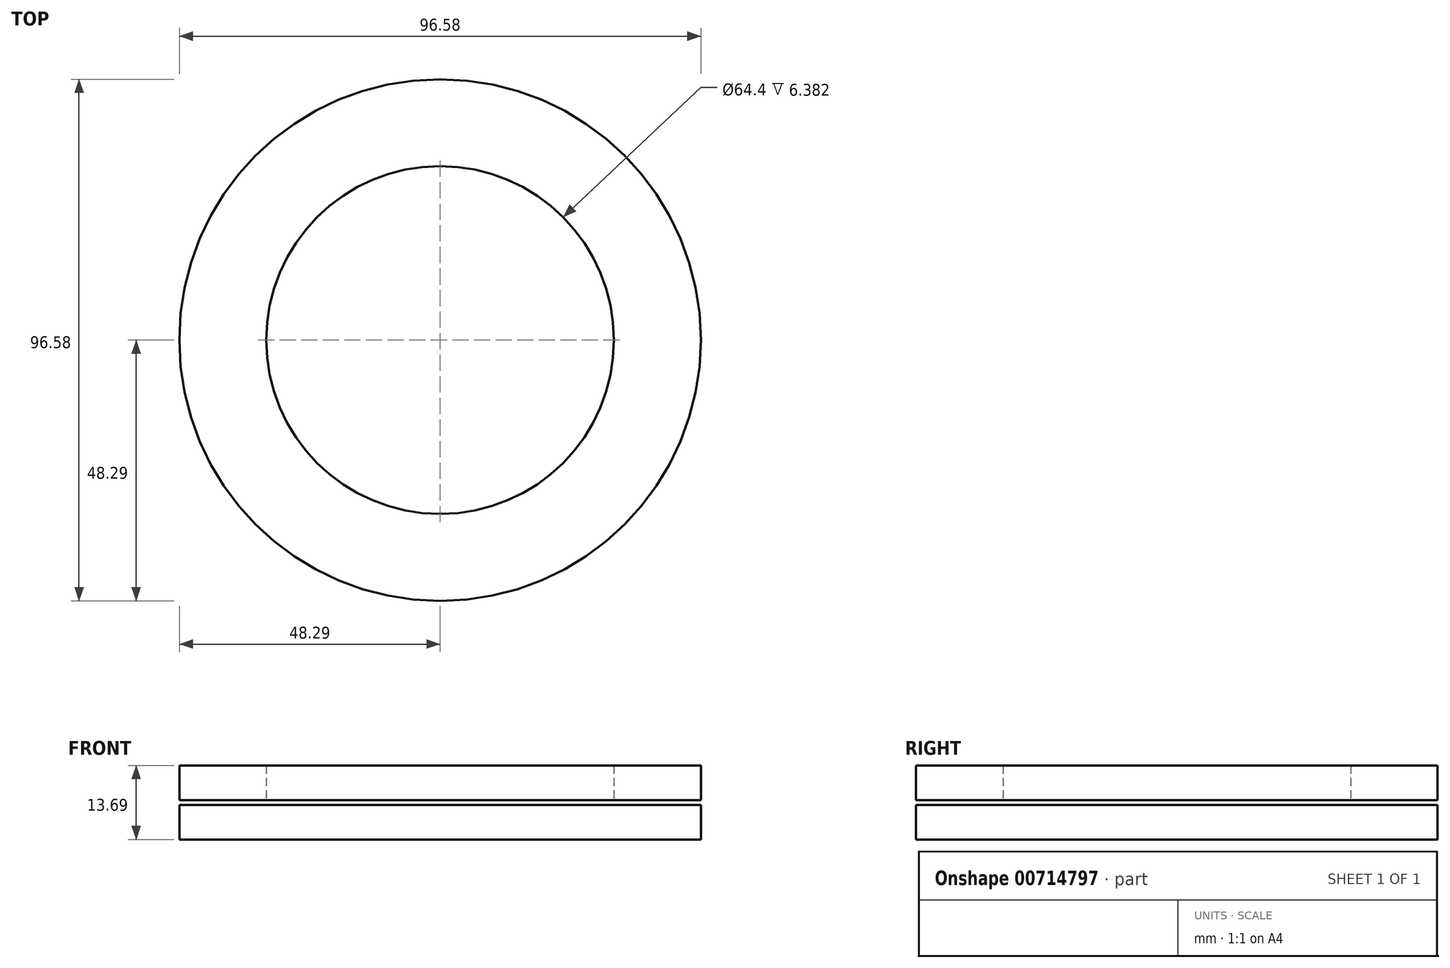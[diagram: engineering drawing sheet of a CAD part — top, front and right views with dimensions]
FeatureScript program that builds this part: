
annotation { "Feature Type Name" : "Feature", "Feature Type Description" : "" }
export const myFeature = defineFeature(function(context is Context, id is Id, definition is map)
    precondition{}
    {
        {
            var Q0;
            Q0=qCreatedBy(makeId("Front.planeOp"),FACE);
            var sketch = newSketch(context, id + "F0", { "sketchPlane" : qUnion([Q0])});
            skLineSegment(sketch, "E0", {"start": v(-60.86, 0) * mm, "end": v(88.25, 0) * mm, "construction": true});
            skLineSegment(sketch, "E1", {"start": v(0, -42.28) * mm, "end": v(0, 45.78) * mm, "construction": true});
            skLineSegment(sketch, "E2.bottom", {"start": v(32.2, 11.83) * mm, "end": v(48.3, 11.83) * mm});
            skLineSegment(sketch, "E2.top", {"start": v(32.2, 18.21) * mm, "end": v(48.3, 18.21) * mm});
            skLineSegment(sketch, "E2.left", {"start": v(32.2, 11.83) * mm, "end": v(32.2, 18.21) * mm});
            skLineSegment(sketch, "E2.right", {"start": v(48.3, 11.83) * mm, "end": v(48.3, 18.21) * mm});
            skLineSegment(sketch, "E3.bottom", {"start": v(48.3, 10.9) * mm, "end": v(0, 10.9) * mm});
            skLineSegment(sketch, "E3.top", {"start": v(48.3, 4.52) * mm, "end": v(0, 4.52) * mm});
            skLineSegment(sketch, "E3.left", {"start": v(48.3, 10.9) * mm, "end": v(48.3, 4.52) * mm});
            skLineSegment(sketch, "E3.right", {"start": v(0, 10.9) * mm, "end": v(0, 4.52) * mm});
            skLineSegment(sketch, "E4.bottom", {"start": v(26.83, 10.9) * mm, "end": v(0, 10.9) * mm});
            skLineSegment(sketch, "E4.left", {"start": v(26.83, 10.9) * mm, "end": v(26.83, 18.21) * mm});
            skLineSegment(sketch, "E4.right", {"start": v(0, 10.9) * mm, "end": v(0, 18.21) * mm});
            skLineSegment(sketch, "E5.left", {"start": v(26.83, 18.21) * mm, "end": v(26.83, 20.8) * mm});
            skLineSegment(sketch, "E5.right", {"start": v(0, 18.21) * mm, "end": v(0, 20.8) * mm});
            skLineSegment(sketch, "E6.bottom", {"start": v(26.83, 20.8) * mm, "end": v(82.15, 20.8) * mm});
            skLineSegment(sketch, "E6.top", {"start": v(0, 26.72) * mm, "end": v(82.15, 26.72) * mm});
            skLineSegment(sketch, "E6.left", {"start": v(0, 20.8) * mm, "end": v(0, 26.72) * mm});
            skLineSegment(sketch, "E6.right", {"start": v(82.15, 20.8) * mm, "end": v(82.15, 26.72) * mm});
            skSolve(sketch);
        }
        {
            var Q0;
            Q0=makeQuery(id+"F0.imprint","IMPRINT",FACE,{"disambiguationData":[TD([[makeQuery(id+"F0.imprint","IMPRINT",EDGE,{"derivedFrom":sQuery(id+"F0.wireOp",EDGE,"E4.bottom")}),-1.0]])]});
            var Q1;
            Q1=makeQuery(id+"F0.imprint","IMPRINT",FACE,{"disambiguationData":[TD([[makeQuery(id+"F0.imprint","IMPRINT",EDGE,{"derivedFrom":sQuery(id+"F0.wireOp",EDGE,"E2.bottom")}),1.0]])]});
            var Q2;
            Q2=makeQuery(id+"F0.imprint","IMPRINT",FACE,{"disambiguationData":[TD([[makeQuery(id+"F0.imprint","IMPRINT",EDGE,{"derivedFrom":sQuery(id+"F0.wireOp",EDGE,"E3.bottom")}),1.0]])]});
            var Q3;
            Q3=sQuery(id+"F0.wireOp",EDGE,"E1");
            revolve(context, id + "F1", {"surfaceOperationType" : NewSurfaceOperationType.NEW, "entities" : qUnion([Q0, Q1, Q2]), "axis" : qUnion([Q3]), "revolveType" : RevolveType.FULL});
        }
    });
